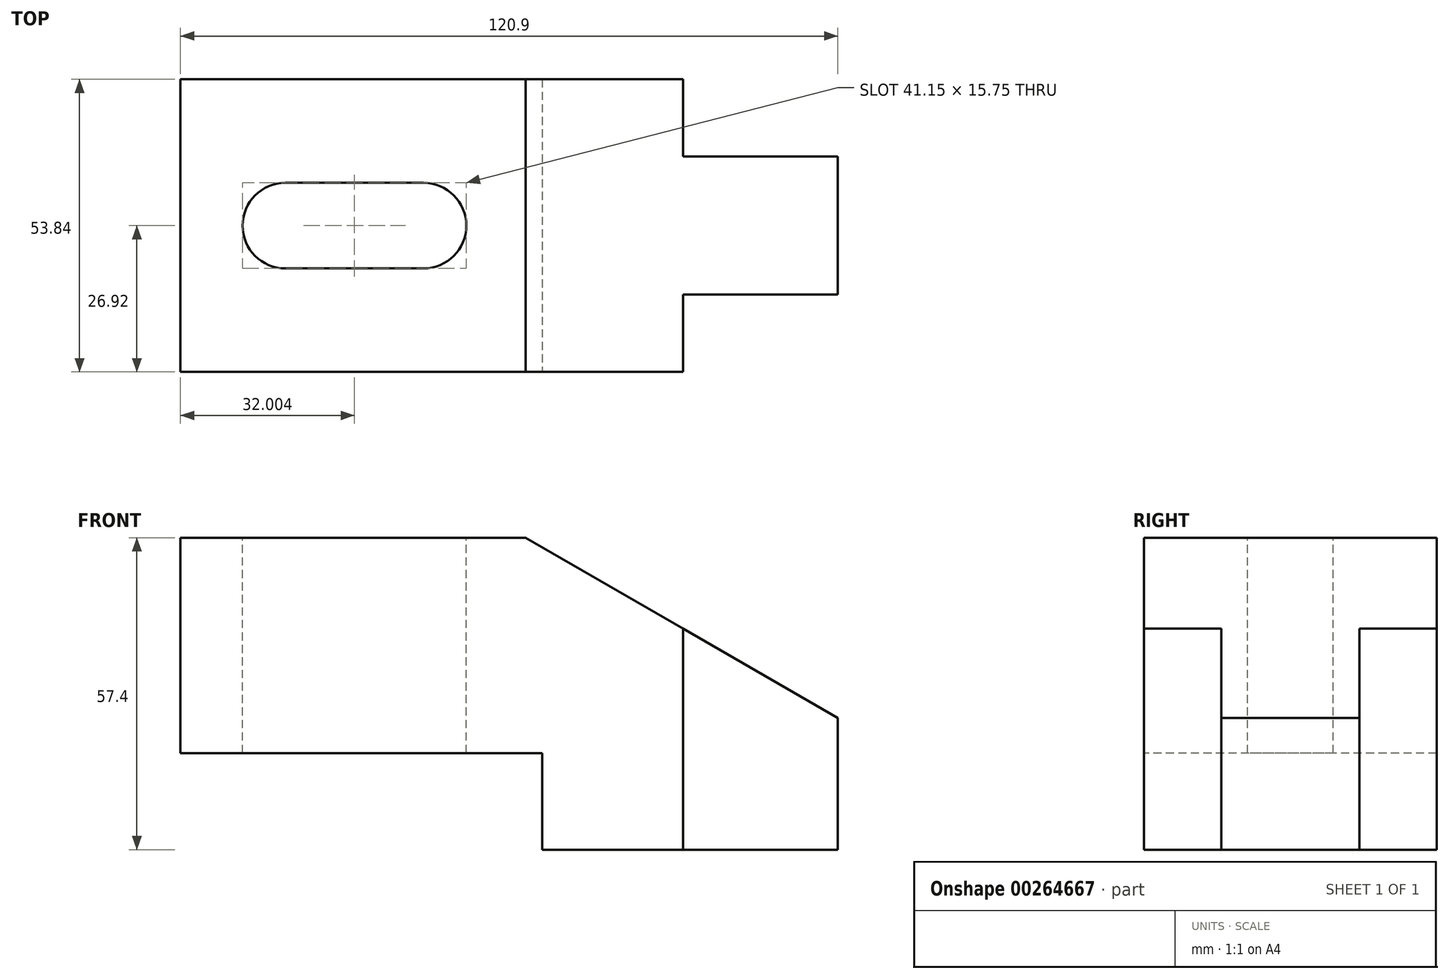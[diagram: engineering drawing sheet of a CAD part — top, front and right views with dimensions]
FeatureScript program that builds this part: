
annotation { "Feature Type Name" : "Feature", "Feature Type Description" : "" }
export const myFeature = defineFeature(function(context is Context, id is Id, definition is map)
    precondition{}
    {
        {
            var Q0;
            Q0=qCreatedBy(makeId("Front.planeOp"),FACE);
            var sketch = newSketch(context, id + "F0", { "sketchPlane" : qUnion([Q0])});
            skLineSegment(sketch, "E0", {"start": v(0, 0) * mm, "end": v(120.9, 0) * mm});
            skLineSegment(sketch, "E1", {"start": v(120.9, 0) * mm, "end": v(120.9, 57.4) * mm});
            skLineSegment(sketch, "E2", {"start": v(120.9, 57.4) * mm, "end": v(0, 57.4) * mm});
            skLineSegment(sketch, "E3", {"start": v(0, 57.4) * mm, "end": v(0, 0) * mm});
            skSolve(sketch);
        }
        {
            var Q0;
            Q0=makeQuery(id+"F0.imprint","IMPRINT",FACE,{"disambiguationData":[TD([[makeQuery(id+"F0.imprint","IMPRINT",EDGE,{"derivedFrom":sQuery(id+"F0.wireOp",EDGE,"E0")}),1.0]])]});
            extrude(context, id + "F1", {"entities" : qUnion([Q0]), "endBound" : BoundingType.SYMMETRIC, "depth" : 53.85 * mm});
        }
        {
            var Q0;
            Q0=makeQuery(id+"F1.opExtrude","CAP_FACE",FACE,{"disambiguationData":[OSD([sQuery(id+"F0.wireOp",EDGE,"E0"),sQuery(id+"F0.wireOp",EDGE,"E1"),sQuery(id+"F0.wireOp",EDGE,"E2"),sQuery(id+"F0.wireOp",EDGE,"E3")])],"isStart":false});
            var sketch = newSketch(context, id + "F2", { "sketchPlane" : qUnion([Q0])});
            skLineSegment(sketch, "E4", {"start": v(0, 0) * mm, "end": v(66.55, 0) * mm});
            skLineSegment(sketch, "E5", {"start": v(0, 57.4) * mm, "end": v(0, 17.78) * mm});
            skLineSegment(sketch, "E6", {"start": v(0, 17.78) * mm, "end": v(66.55, 17.78) * mm});
            skLineSegment(sketch, "E7", {"start": v(66.55, 17.78) * mm, "end": v(66.55, 0) * mm});
            skLineSegment(sketch, "E8", {"start": v(0, 57.4) * mm, "end": v(63.5, 57.4) * mm});
            skLineSegment(sketch, "E9", {"start": v(120.9, 24.26) * mm, "end": v(63.5, 57.4) * mm});
            skSolve(sketch);
        }
        {
            var Q0;
            {var subQ0=sQuery(id+"F2.wireOp",EDGE,"E4");Q0=makeQuery(id+"F2.imprint","IMPRINT",FACE,{"disambiguationData":[TD([[makeQuery(id+"F2.imprint","IMPRINT",EDGE,{"derivedFrom":subQ0}),1.0]])]});}
            var Q1;
            {var subQ0=sQuery(id+"F2.wireOp",EDGE,"E9");Q1=makeQuery(id+"F2.imprint","IMPRINT",FACE,{"disambiguationData":[TD([[makeQuery(id+"F2.imprint","IMPRINT",EDGE,{"derivedFrom":subQ0}),-1.0]])]});}
            extrude(context, id + "F3", {"entities" : qUnion([Q0, Q1]), "operationType" : NewBodyOperationType.REMOVE, "endBound" : BoundingType.THROUGH_ALL, "oppositeDirection" : true, "depth" : 25.4 * mm});
        }
        {
            var Q0;
            Q0=makeQuery(id+"F1.opExtrude","SWEPT_FACE",FACE,{"disambiguationData":[OSD([sQuery(id+"F0.wireOp",EDGE,"E0")])]});
            var sketch = newSketch(context, id + "F4", { "sketchPlane" : qUnion([Q0])});
            skLineSegment(sketch, "E10", {"start": v(120.9, -26.92) * mm, "end": v(120.9, -12.7) * mm});
            skLineSegment(sketch, "E11", {"start": v(120.9, -12.7) * mm, "end": v(92.46, -12.7) * mm});
            skLineSegment(sketch, "E12", {"start": v(92.46, -12.7) * mm, "end": v(92.46, -26.92) * mm});
            skLineSegment(sketch, "E13", {"start": v(120.9, 26.92) * mm, "end": v(120.9, 12.7) * mm});
            skLineSegment(sketch, "E14", {"start": v(120.9, 12.7) * mm, "end": v(92.46, 12.7) * mm});
            skLineSegment(sketch, "E15", {"start": v(92.46, 12.7) * mm, "end": v(92.46, 26.92) * mm});
            skSolve(sketch);
        }
        {
            var Q0;
            {var subQ0=sQuery(id+"F4.wireOp",EDGE,"E13");Q0=makeQuery(id+"F4.imprint","IMPRINT",FACE,{"disambiguationData":[TD([[makeQuery(id+"F4.imprint","IMPRINT",EDGE,{"derivedFrom":subQ0}),-1.0]])]});}
            var Q1;
            {var subQ0=sQuery(id+"F4.wireOp",EDGE,"E10");Q1=makeQuery(id+"F4.imprint","IMPRINT",FACE,{"disambiguationData":[TD([[makeQuery(id+"F4.imprint","IMPRINT",EDGE,{"derivedFrom":subQ0}),-1.0]])]});}
            extrude(context, id + "F5", {"entities" : qUnion([Q0, Q1]), "operationType" : NewBodyOperationType.REMOVE, "endBound" : BoundingType.THROUGH_ALL, "oppositeDirection" : true, "depth" : 25.4 * mm});
        }
        {
            var Q0;
            Q0=makeQuery(id+"F1.opExtrude","SWEPT_FACE",FACE,{"disambiguationData":[OSD([sQuery(id+"F0.wireOp",EDGE,"E2")])]});
            var sketch = newSketch(context, id + "F6", { "sketchPlane" : qUnion([Q0])});
            skLineSegment(sketch, "E16", {"start": v(0, 0) * mm, "end": v(0, -26.92) * mm});
            skLineSegment(sketch, "E17", {"start": v(0, 0) * mm, "end": v(19.3, 0) * mm});
            skLineSegment(sketch, "E18", {"start": v(19.3, 0) * mm, "end": v(44.7, 0) * mm});
            skCircle(sketch, "E19", {"center": v(19.3, 0) * mm, "radius": 7.87 * mm});
            skCircle(sketch, "E20", {"center": v(44.7, 0) * mm, "radius": 7.87 * mm});
            skLineSegment(sketch, "E21", {"start": v(19.3, -7.87) * mm, "end": v(44.7, -7.87) * mm});
            skLineSegment(sketch, "E22", {"start": v(19.3, 7.87) * mm, "end": v(44.7, 7.87) * mm});
            skSolve(sketch);
        }
        {
            var Q0;
            {var subQ5=sQuery(id+"F6.wireOp",EDGE,"E21");Q0=makeQuery(id+"F6.imprint","IMPRINT",FACE,{"disambiguationData":[TD([[makeQuery(id+"F6.imprint","IMPRINT",EDGE,{"derivedFrom":subQ5}),1.0]])]});}
            var Q1;
            {var subQ5=sQuery(id+"F6.wireOp",EDGE,"E22");Q1=makeQuery(id+"F6.imprint","IMPRINT",FACE,{"disambiguationData":[TD([[makeQuery(id+"F6.imprint","IMPRINT",EDGE,{"derivedFrom":subQ5}),-1.0]])]});}
            var Q2;
            {var subQ0=sQuery(id+"F6.wireOp",EDGE,"E18");var subQ1=sQuery(id+"F6.wireOp",EDGE,"E17");var subQ2=makeQuery(id+"F6.imprint","INTERSECT",VERTEX,{"derivedFrom":[subQ1,subQ0]});Q2=makeQuery(id+"F6.imprint","IMPRINT",FACE,{"disambiguationData":[TD([[makeQuery(id+"F6.imprint","IMPRINT",EDGE,{"disambiguationData":[TD([[subQ2,1.0]])],"derivedFrom":subQ1}),1.0]])]});}
            var Q3;
            {var subQ0=sQuery(id+"F6.wireOp",EDGE,"E18");var subQ1=sQuery(id+"F6.wireOp",EDGE,"E17");var subQ2=makeQuery(id+"F6.imprint","INTERSECT",VERTEX,{"derivedFrom":[subQ1,subQ0]});Q3=makeQuery(id+"F6.imprint","IMPRINT",FACE,{"disambiguationData":[TD([[makeQuery(id+"F6.imprint","IMPRINT",EDGE,{"disambiguationData":[TD([[subQ2,1.0]])],"derivedFrom":subQ1}),-1.0]])]});}
            var Q4;
            {var subQ0=sQuery(id+"F6.wireOp",EDGE,"E20");var subQ1=makeQuery(id+"F6.imprint","INTERSECT",VERTEX,{"derivedFrom":[subQ0,sQuery(id+"F6.wireOp",EDGE,"E22")]});Q4=makeQuery(id+"F6.imprint","IMPRINT",FACE,{"disambiguationData":[TD([[makeQuery(id+"F6.imprint","IMPRINT",EDGE,{"disambiguationData":[TD([[subQ1,-1.0]])],"derivedFrom":subQ0}),1.0]])]});}
            extrude(context, id + "F7", {"entities" : qUnion([Q0, Q1, Q2, Q3, Q4]), "operationType" : NewBodyOperationType.REMOVE, "endBound" : BoundingType.THROUGH_ALL, "oppositeDirection" : true, "depth" : 25.4 * mm});
        }
    });
